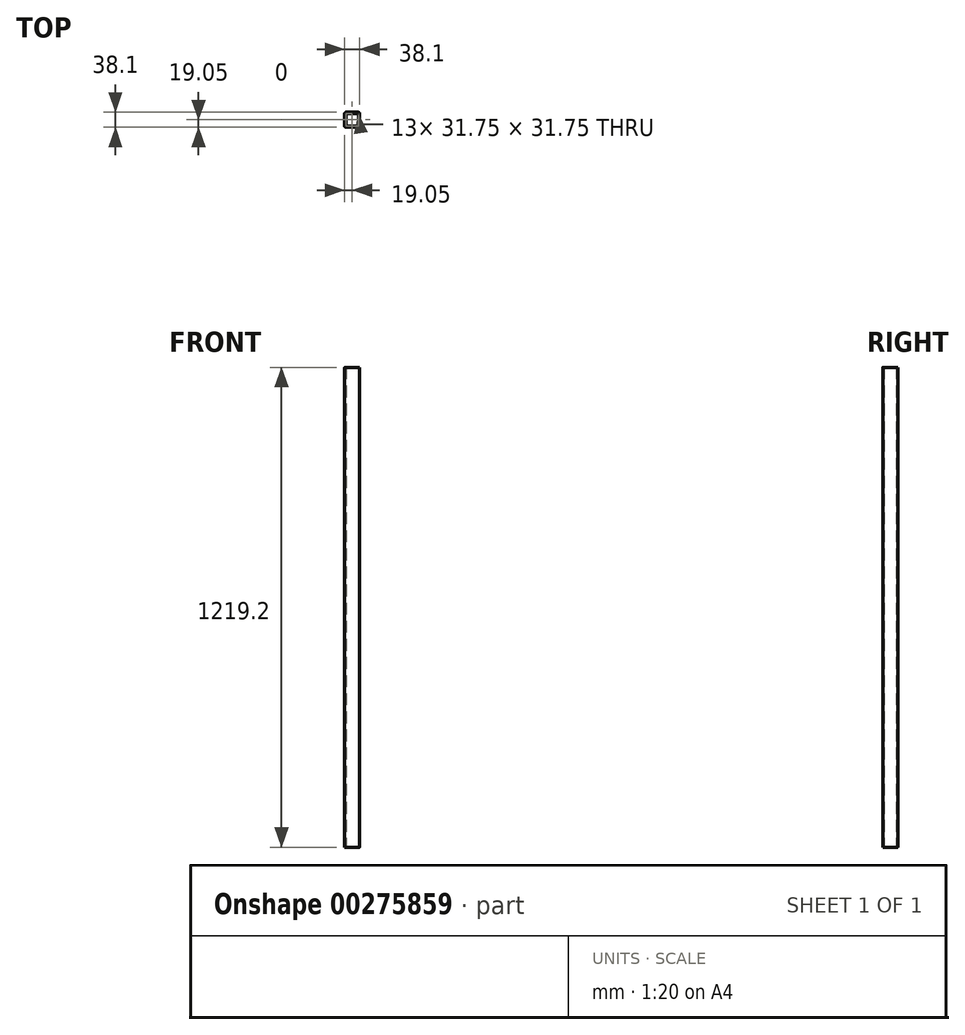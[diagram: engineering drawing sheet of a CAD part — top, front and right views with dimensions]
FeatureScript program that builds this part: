
annotation { "Feature Type Name" : "Feature", "Feature Type Description" : "" }
export const myFeature = defineFeature(function(context is Context, id is Id, definition is map)
    precondition{}
    {
        {
            var Q0;
            Q0=qCreatedBy(makeId("Top.planeOp"),FACE);
            var sketch = newSketch(context, id + "F0", { "sketchPlane" : qUnion([Q0])});
            skLineSegment(sketch, "E0.bottom", {"start": v(15.88, -19.05) * mm, "end": v(-15.87, -19.05) * mm});
            skLineSegment(sketch, "E0.top", {"start": v(15.87, 19.05) * mm, "end": v(-15.88, 19.05) * mm});
            skLineSegment(sketch, "E0.left", {"start": v(19.05, -15.87) * mm, "end": v(19.05, 15.88) * mm});
            skLineSegment(sketch, "E0.right", {"start": v(-19.05, -15.88) * mm, "end": v(-19.05, 15.87) * mm});
            skPoint(sketch, "E0.middle", {"position": v(0, 0) * mm});
            skPoint(sketch, "E1.visualSharp", {"position": v(-19.05, 19.05) * mm});
            skArc(sketch, "E1.filletArc", {"start": v(-15.88, 19.05) * mm, "mid": v(-18.12, 18.12) * mm, "end": v(-19.05, 15.87) * mm});
            skPoint(sketch, "E2.visualSharp", {"position": v(19.05, 19.05) * mm});
            skArc(sketch, "E2.filletArc", {"start": v(19.05, 15.88) * mm, "mid": v(18.12, 18.12) * mm, "end": v(15.87, 19.05) * mm});
            skPoint(sketch, "E3.visualSharp", {"position": v(-19.05, -19.05) * mm});
            skArc(sketch, "E3.filletArc", {"start": v(-19.05, -15.88) * mm, "mid": v(-18.12, -18.12) * mm, "end": v(-15.87, -19.05) * mm});
            skPoint(sketch, "E4.visualSharp", {"position": v(19.05, -19.05) * mm});
            skArc(sketch, "E4.filletArc", {"start": v(15.88, -19.05) * mm, "mid": v(18.12, -18.12) * mm, "end": v(19.05, -15.87) * mm});
            skLineSegment(sketch, "E5.bottom", {"start": v(-15.88, 15.87) * mm, "end": v(15.88, 15.87) * mm});
            skLineSegment(sketch, "E5.top", {"start": v(-15.88, -15.87) * mm, "end": v(15.88, -15.87) * mm});
            skLineSegment(sketch, "E5.left", {"start": v(-15.88, 15.87) * mm, "end": v(-15.88, -15.87) * mm});
            skLineSegment(sketch, "E5.right", {"start": v(15.88, 15.87) * mm, "end": v(15.88, -15.87) * mm});
            skSolve(sketch);
        }
        {
            var Q0;
            Q0 = qSketchRegion(id + "F0", true);
            extrude(context, id + "F1", {"entities" : qUnion([Q0]), "depth" : 1219.2 * mm});
        }
    });
